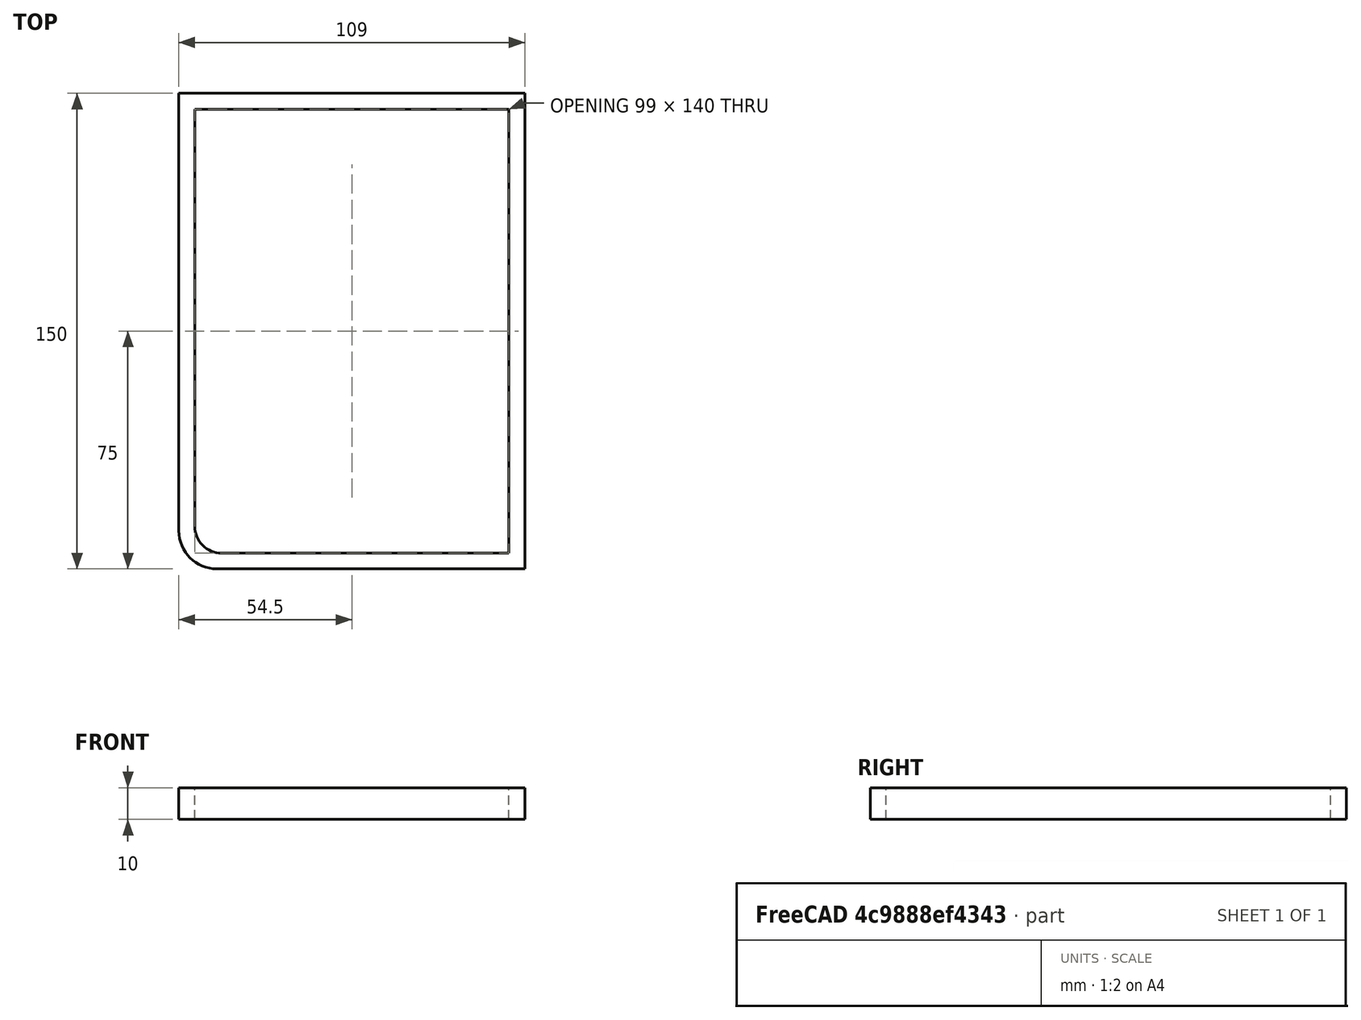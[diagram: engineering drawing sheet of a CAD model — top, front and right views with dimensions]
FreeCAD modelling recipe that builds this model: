
FCSTD DOCUMENT  (FreeCAD 1.0R38806 (Git))
Label: CheeseCutter 3
License: All rights reserved
LicenseURL: https://en.wikipedia.org/wiki/All_rights_reserved
objects: Sketcher::SketchObject×1, PartDesign::Pad×1, PartDesign::Body×1
note: 6 computed .brp shape members not serialized (recipe doc carries the construction recipe); baked Part::Feature solids carry a one-line shape summary decoded from their .brp

FEATURE [Sketcher::SketchObject] Sketch
  ArcFitTolerance = 1e-06
  AttachmentSupport = -> [XY_Plane]
  FullyConstrained = false
  MakeInternals = false
  MapMode = 5
  sketch-geometry (17):
    g0: LineSegment StartX=-41.0551 StartY=-70 StartZ=0 EndX=49.5 EndY=-70 EndZ=0
    g1: LineSegment StartX=49.5 StartY=-70 StartZ=0 EndX=49.5 EndY=70 EndZ=0
    g2: LineSegment StartX=49.5 StartY=70 StartZ=0 EndX=-49.5 EndY=70 EndZ=0
    g3: LineSegment StartX=-49.5 StartY=70 StartZ=0 EndX=-49.5 EndY=-61.5551 EndZ=0
    g4: LineSegment StartX=-42.4693 StartY=-75 StartZ=0 EndX=54.5 EndY=-75 EndZ=0
    g5: LineSegment StartX=54.5 StartY=-75 StartZ=0 EndX=54.5 EndY=75 EndZ=0
    g6: LineSegment StartX=54.5 StartY=75 StartZ=0 EndX=-54.5 EndY=75 EndZ=0
    g7: LineSegment StartX=-54.5 StartY=75 StartZ=0 EndX=-54.5 EndY=-62.9693 EndZ=0
    g8: LineSegment [constr] StartX=-49.5 StartY=-70 StartZ=0 EndX=-54.5 EndY=-75 EndZ=0
    g9: LineSegment [constr] StartX=49.5 StartY=-70 StartZ=0 EndX=54.5 EndY=-75 EndZ=0
    g10: LineSegment [constr] StartX=49.5 StartY=70 StartZ=0 EndX=54.5 EndY=75 EndZ=0
    g11: LineSegment [constr] StartX=-49.5 StartY=70 StartZ=0 EndX=-54.5 EndY=75 EndZ=0
    g12: GeomPoint [constr] X=0 Y=0 Z=0
    g13: ArcOfCircle CenterX=-42.4693 CenterY=-62.9693 CenterZ=0 NormalX=0 NormalY=0 NormalZ=1 AngleXU=0 Radius=12.0307 StartAngle=3.14159 EndAngle=4.71239
    g14: GeomPoint [constr] X=-54.5 Y=-75 Z=0
    g15: ArcOfCircle CenterX=-41.0551 CenterY=-61.5551 CenterZ=0 NormalX=0 NormalY=0 NormalZ=1 AngleXU=0 Radius=8.4449 StartAngle=3.14159 EndAngle=4.71239
    g16: GeomPoint [constr] X=-49.5 Y=-70 Z=0
  constraints (39):
    c: Coincident(g0,g1)
    c: Coincident(g1,g2)
    c: Coincident(g2,g3)
    c: Horizontal(g0)
    c: Horizontal(g2)
    c: Vertical(g1)
    c: Vertical(g3)
    c: Coincident(g4,g5)
    c: Coincident(g5,g6)
    c: Coincident(g6,g7)
    c: Horizontal(g4)
    c: Horizontal(g6)
    c: Vertical(g5)
    c: Vertical(g7)
    c: Coincident(g8,g16)
    c: Coincident(g8,g14)
    c: Coincident(g9,g1)
    c: Coincident(g9,g5)
    c: Coincident(g10,g2)
    c: Coincident(g10,g6)
    c: Coincident(g11,g3)
    c: Coincident(g11,g7)
    c: Perpendicular(g8,g9)
    c: Perpendicular(g9,g10)
    c: Perpendicular(g10,g11)
    c: Symmetric(g2,g16,g12)
    c: Distance(g1,g16) = 99
    c: Distance(g16,g2) = 140
    c: Distance(g14,g0) = 5  'distWall'
    c: Coincident(g12,g-1)
    c: PointOnObject(g14,g7)
    c: PointOnObject(g14,g4)
    c: Tangent(g7,g13) = -1.5708
    c: Tangent(g4,g13) = -1.5708
    c: PointOnObject(g16,g3)
    c: PointOnObject(g16,g0)
    c: Tangent(g3,g15) = -1.5708
    c: Tangent(g0,g15) = -1.5708
    c: Distance(g13,g15) = 2
FEATURE [PartDesign::Pad] Pad
  Direction = (0,0,1)
  Length = 10
  Length2 = 10
  Midplane = true
  Profile = -> Sketch
  ReferenceAxis = -> Sketch [N_Axis]
  Refine = true
  Suppressed = false
  Type = 0
FEATURE [PartDesign::Body] Body
  AllowCompound = false
  Group = -> [Sketch,Pad]
  Origin = -> Origin
  Tip = -> Pad
